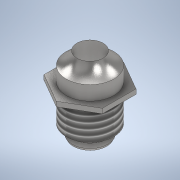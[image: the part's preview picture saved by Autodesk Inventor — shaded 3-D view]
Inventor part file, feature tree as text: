
AUTODESK INVENTOR PART (.ipt)
format: ipt  version: 2022 (Build 260153000, 153)  size: 184,320 bytes
history: native  units: mm
features: sketch x9, extrude x6, plane x2, loft x2, projected_geometry x2, other x2, fillet x1, thread x1
ambient origin geometry x8: Origin, YZ Plane, XZ Plane, XY Plane, X Axis, Y Axis, Z Axis, Center Point
bodies: Solid1 (feature_tree)
feature tree (25):
  extrude  "Extrusion1"  Depth=20.0mm
  extrude  "Extrusion2"  Depth=2.0mm TaperAngle=0.0deg
  extrude  "Extrusion3"  Depth=9.5mm TaperAngle=0.0deg
  fillet  "Fillet1"  Radius=9.5mm
  extrude  "Extrusion4"  Depth=13.0mm TaperAngle=0.0deg
  thread  "Thread1"  [1 undecoded]
  plane  "Work Plane1"
  loft  "Loft1"
  extrude  "Extrusion5"  Depth=2.0mm TaperAngle=0.0deg
  plane  "Work Plane2"
  loft  "Loft2"
  extrude  "Extrusion6"  TaperAngle=0.0deg  [1 undecoded]
  sketch  "Sketch9"  dims[d28=11.0mm d29=0.0mm d30=0.0mm]
  sketch  "Sketch1"  dims[d0=12.25mm d1=20.0mm]
  sketch  "Sketch2"  dims[d2=2.0mm d3=0.0mm d4=8.0mm d5=0.0mm]
  sketch  "Sketch3"  dims[d6=10.0mm d7=8.0mm d8=0.0mm d9=9.5mm]
  sketch  "Sketch4"  dims[d10=13.0mm d11=0.0mm d12=13.0mm d13=0.0mm d14=2.0mm]
  projected_geometry  "Projected Loop1"
  sketch  "Sketch5"  dims[d15=15.0mm d16=0.0mm d17=90.0deg]
  other  "Edges1"
  sketch  "Sketch6"  dims[d18=0.0mm d19=90.0deg d20=2.0mm d21=0.0mm]
  projected_geometry  "Projected Loop2"
  sketch  "Sketch7"  dims[d22=1.0mm d23=14.0mm]
  other  "Edges2"
  sketch  "Sketch8"  dims[d24=0.0mm d25=90.0deg d26=0.0mm d27=90.0deg]
note: 2 required parameter values undecoded (feature->parameter linkage not recoverable at this tier; creation-order binding heuristic only, values carry confidence <= 0.55)
